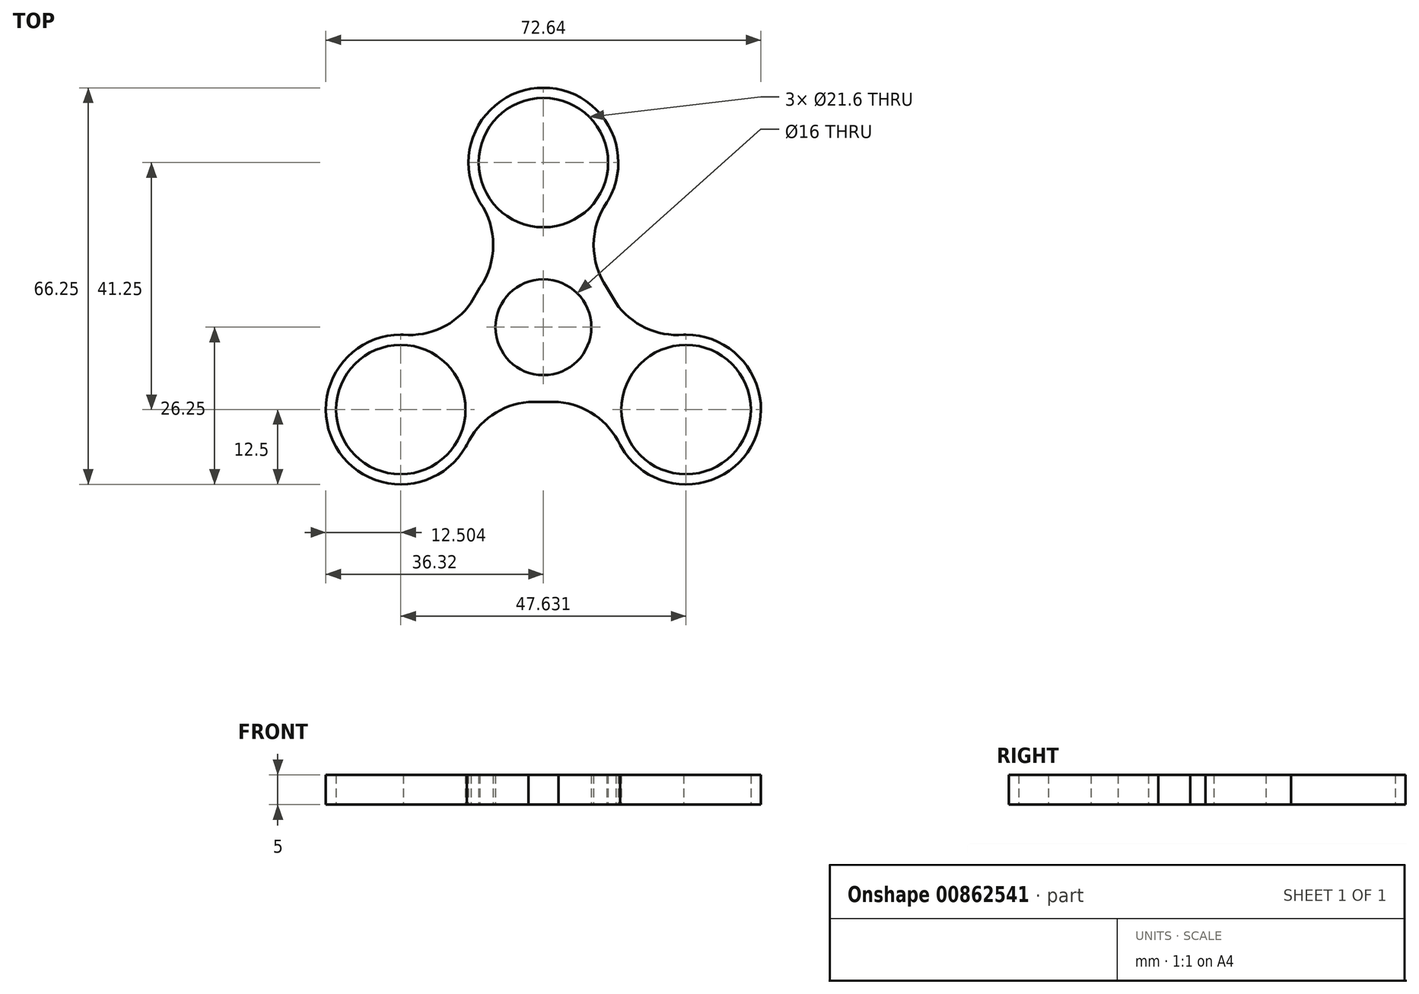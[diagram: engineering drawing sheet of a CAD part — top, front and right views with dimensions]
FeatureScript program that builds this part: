
annotation { "Feature Type Name" : "Feature", "Feature Type Description" : "" }
export const myFeature = defineFeature(function(context is Context, id is Id, definition is map)
    precondition{}
    {
        {
            var Q0;
            Q0=qCreatedBy(makeId("Top.planeOp"),FACE);
            var sketch = newSketch(context, id + "F0", { "sketchPlane" : qUnion([Q0])});
            skCircle(sketch, "E0", {"center": v(0, 0) * mm, "radius": 8 * mm});
            skCircle(sketch, "E1.cCircle", {"center": v(0, 0) * mm, "radius": 12.5 * mm, "construction": true});
            skLineSegment(sketch, "E1.0", {"start": v(-7.22, 12.5) * mm, "end": v(7.22, 12.5) * mm});
            skLineSegment(sketch, "E1.1", {"start": v(7.22, 12.5) * mm, "end": v(14.43, 0) * mm});
            skLineSegment(sketch, "E1.2", {"start": v(14.43, 0) * mm, "end": v(7.22, -12.5) * mm});
            skLineSegment(sketch, "E1.3", {"start": v(7.22, -12.5) * mm, "end": v(-7.22, -12.5) * mm});
            skLineSegment(sketch, "E1.4", {"start": v(-7.22, -12.5) * mm, "end": v(-14.43, 0) * mm});
            skLineSegment(sketch, "E1.5", {"start": v(-14.43, 0) * mm, "end": v(-7.22, 12.5) * mm});
            skPoint(sketch, "E1.0.midPoint", {"position": v(0, 12.5) * mm});
            skCircle(sketch, "E2.cCircle", {"center": v(0, 27.5) * mm, "radius": 12.5 * mm});
            skLineSegment(sketch, "E2.0", {"start": v(-7.22, 40) * mm, "end": v(7.22, 40) * mm});
            skLineSegment(sketch, "E2.1", {"start": v(7.22, 40) * mm, "end": v(14.43, 27.5) * mm, "construction": true});
            skLineSegment(sketch, "E2.2", {"start": v(14.43, 27.5) * mm, "end": v(7.22, 15) * mm});
            skLineSegment(sketch, "E2.3", {"start": v(7.22, 15) * mm, "end": v(-7.22, 15) * mm});
            skLineSegment(sketch, "E2.4", {"start": v(-7.22, 15) * mm, "end": v(-14.43, 27.5) * mm});
            skLineSegment(sketch, "E2.5", {"start": v(-14.43, 27.5) * mm, "end": v(-7.22, 40) * mm});
            skPoint(sketch, "E2.0.midPoint", {"position": v(0, 40) * mm});
            skCircle(sketch, "E3.cCircle", {"center": v(0, 27.5) * mm, "radius": 10.8 * mm});
            skLineSegment(sketch, "E3.0", {"start": v(-6.24, 38.3) * mm, "end": v(6.24, 38.3) * mm, "construction": true});
            skLineSegment(sketch, "E3.1", {"start": v(6.24, 38.3) * mm, "end": v(12.47, 27.5) * mm});
            skLineSegment(sketch, "E3.2", {"start": v(12.47, 27.5) * mm, "end": v(6.24, 16.7) * mm, "construction": true});
            skLineSegment(sketch, "E3.3", {"start": v(6.24, 16.7) * mm, "end": v(-6.24, 16.7) * mm});
            skLineSegment(sketch, "E3.4", {"start": v(-6.24, 16.7) * mm, "end": v(-12.47, 27.5) * mm, "construction": true});
            skLineSegment(sketch, "E3.5", {"start": v(-12.47, 27.5) * mm, "end": v(-6.24, 38.3) * mm});
            skPoint(sketch, "E3.0.midPoint", {"position": v(0, 38.3) * mm});
            skLineSegment(sketch, "E4", {"start": v(7.22, 15) * mm, "end": v(7.22, 12.5) * mm});
            skLineSegment(sketch, "E5", {"start": v(-7.22, 12.5) * mm, "end": v(-7.22, 15) * mm});
            skCircle(sketch, "E6", {"center": v(20.88, 13.75) * mm, "radius": 12.5 * mm});
            skPoint(sketch, "E6.centerSnap0", {"position": v(7.22, 13.75) * mm});
            skLineSegment(sketch, "E7", {"start": v(0, 12.5) * mm, "end": v(0, 15) * mm, "construction": true});
            skCircle(sketch, "E8.MirrorC", {"center": v(-20.88, 13.75) * mm, "radius": 12.5 * mm});
            skLineSegment(sketch, "E9", {"start": v(14.43, 0) * mm, "end": v(26.22, 0) * mm, "construction": true});
            skSolve(sketch);
        }
        {
            var Q0;
            Q0=makeQuery(id+"F0.imprint","IMPRINT",FACE,{"disambiguationData":[TD([[makeQuery(id+"F0.imprint","IMPRINT",EDGE,{"derivedFrom":sQuery(id+"F0.wireOp",EDGE,"E0")}),-1.0]])]});
            extrude(context, id + "F1", {"entities" : qUnion([Q0]), "depth" : 5 * mm, "offsetDistance" : 25 * mm});
        }
        {
            var Q0;
            Q0=makeQuery(id+"F0.imprint","IMPRINT",FACE,{"disambiguationData":[TD([[makeQuery(id+"F0.imprint","IMPRINT",EDGE,{"derivedFrom":sQuery(id+"F0.wireOp",EDGE,"E1.0")}),1.0]])]});
            var Q1;
            Q1=makeQuery(id+"F0.imprint","IMPRINT",FACE,{"disambiguationData":[TD([[makeQuery(id+"F0.imprint","IMPRINT",EDGE,{"derivedFrom":sQuery(id+"F0.wireOp",EDGE,"E3.0")}),1.0]])]});
            var Q2;
            {var subQ0=sQuery(id+"F0.wireOp",EDGE,"E2.2");var subQ1=sQuery(id+"F0.wireOp",EDGE,"E2.cCircle");var subQ2=makeQuery(id+"F0.imprint","INTERSECT",VERTEX,{"derivedFrom":[subQ1,subQ0]});Q2=makeQuery(id+"F0.imprint","IMPRINT",FACE,{"disambiguationData":[TD([[makeQuery(id+"F0.imprint","IMPRINT",EDGE,{"disambiguationData":[TD([[subQ2,1.0]])],"derivedFrom":subQ1}),-1.0]])]});}
            var Q3;
            {var subQ0=sQuery(id+"F0.wireOp",EDGE,"E2.4");var subQ1=sQuery(id+"F0.wireOp",EDGE,"E2.cCircle");var subQ2=makeQuery(id+"F0.imprint","INTERSECT",VERTEX,{"derivedFrom":[subQ1,subQ0]});Q3=makeQuery(id+"F0.imprint","IMPRINT",FACE,{"disambiguationData":[TD([[makeQuery(id+"F0.imprint","IMPRINT",EDGE,{"disambiguationData":[TD([[subQ2,-1.0]])],"derivedFrom":subQ1}),-1.0]])]});}
            var Q4;
            {var subQ0=sQuery(id+"F0.wireOp",EDGE,"E2.3");var subQ1=sQuery(id+"F0.wireOp",EDGE,"E2.cCircle");var subQ2=makeQuery(id+"F0.imprint","INTERSECT",VERTEX,{"derivedFrom":[subQ1,subQ0]});Q4=makeQuery(id+"F0.imprint","IMPRINT",FACE,{"disambiguationData":[TD([[makeQuery(id+"F0.imprint","IMPRINT",EDGE,{"disambiguationData":[TD([[subQ2,-1.0]])],"derivedFrom":subQ1}),-1.0]])]});}
            var Q5;
            {var subQ0=sQuery(id+"F0.wireOp",EDGE,"E8.MirrorC");var subQ1=sQuery(id+"F0.wireOp",EDGE,"E2.cCircle");var subQ2=makeQuery(id+"F0.imprint","INTERSECT",VERTEX,{"derivedFrom":[subQ1,subQ0]});Q5=makeQuery(id+"F0.imprint","IMPRINT",FACE,{"disambiguationData":[TD([[makeQuery(id+"F0.imprint","IMPRINT",EDGE,{"disambiguationData":[TD([[subQ2,-1.0]])],"derivedFrom":subQ1}),-1.0]])]});}
            var Q6;
            {var subQ0=sQuery(id+"F0.wireOp",EDGE,"E5");Q6=makeQuery(id+"F0.imprint","IMPRINT",FACE,{"disambiguationData":[TD([[makeQuery(id+"F0.imprint","IMPRINT",EDGE,{"derivedFrom":subQ0}),1.0]])]});}
            var Q7;
            {var subQ0=sQuery(id+"F0.wireOp",EDGE,"E4");Q7=makeQuery(id+"F0.imprint","IMPRINT",FACE,{"disambiguationData":[TD([[makeQuery(id+"F0.imprint","IMPRINT",EDGE,{"derivedFrom":subQ0}),1.0]])]});}
            var Q8;
            {var subQ8=sQuery(id+"F0.wireOp",EDGE,"E3.cCircle");var subQ9=makeQuery(id+"F0.imprint","IMPRINT",VERTEX,{"disambiguationData":[OD(0.0)],"derivedFrom":subQ8});Q8=makeQuery(id+"F0.imprint","IMPRINT",FACE,{"disambiguationData":[TD([[makeQuery(id+"F0.imprint","IMPRINT",EDGE,{"disambiguationData":[TD([[subQ9,1.0]])],"derivedFrom":subQ8}),-1.0]])]});}
            extrude(context, id + "F2", {"entities" : qUnion([Q0, Q1, Q2, Q3, Q4, Q5, Q6, Q7, Q8]), "depth" : 5 * mm, "offsetDistance" : 25 * mm});
        }
        {
            var Q0;
            Q0=makeQuery(id+"F2.opExtrude","SWEPT_BODY",BODY,{"disambiguationData":[OSD([sQuery(id+"F0.wireOp",EDGE,"E2.0"),sQuery(id+"F0.wireOp",EDGE,"E2.1"),sQuery(id+"F0.wireOp",EDGE,"E2.2"),sQuery(id+"F0.wireOp",EDGE,"E2.3"),sQuery(id+"F0.wireOp",EDGE,"E2.4"),sQuery(id+"F0.wireOp",EDGE,"E2.5"),sQuery(id+"F0.wireOp",EDGE,"E3.0"),sQuery(id+"F0.wireOp",EDGE,"E3.1"),sQuery(id+"F0.wireOp",EDGE,"E3.2"),sQuery(id+"F0.wireOp",EDGE,"E3.3"),sQuery(id+"F0.wireOp",EDGE,"E3.4"),sQuery(id+"F0.wireOp",EDGE,"E3.5")])]});
            var Q1;
            Q1=sQuery(id+"F0.wireOp",EDGE,"E1.cCircle");
            circularPattern(context, id + "F3", {"operationType" : NewBodyOperationType.ADD, "entities" : qUnion([Q0]), "axis" : qUnion([Q1]), "angle" : 360 * degree, "instanceCount" : 3, "equalSpace" : true});
        }
    });
